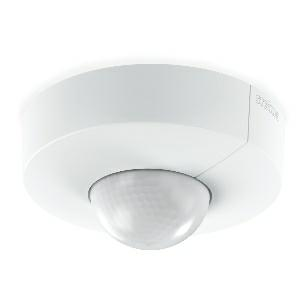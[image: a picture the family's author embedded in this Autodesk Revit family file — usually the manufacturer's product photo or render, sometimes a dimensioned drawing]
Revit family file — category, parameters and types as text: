
# Revit family: is_345_033859
name_source: partatom
category: Elektroinstallationen
revit_build: Autodesk Revit 2016 (Build: 20190508_0715(x64)
units: mm (PartAtom-declared; Revit-internal decimal feet)

## family parameters
Basisbauteil = Fläche
Beim Laden mit Abzugskörper schneiden = Nein
Bemaßung runder Anschluss = Durchmesser verwenden
Beschriftungsausrichtung beibehalten = Nein
Gemeinsam genutzt = Nein
Raumberechnungspunkt = Nein
Teiletyp = Normal

## types (1)
- IS 345
    Apparent Load = 0 VA
    Beschreibung = Type: Motion detectors; Dimensions (Ø x H): 126 x 65 mm; Mains power supply: 220 – 240 V / 50 – 60 Hz; Sensor Technology: passive infrared; Application, place: Outdoors, Indoors; Application, room: corridor / aisle, multi-storey / underground car park, outdoors, hotel room; Installation site: ceiling; Installation: Surface wiring; Switching zones: 280 switching zones; Electronic scalability: No; Mechanical scalability: No; Mounting height: 2,50 – 5,00 m; Optimum mounting height: 2,8 m; Detection angle: 360 °; Angle of aperture: 45 °; Sneak-by guard: Yes; Capability of masking out individual segments: Yes; Reach, radial: 12 x 6 m (72 m²); Reach, tangential: 23 x 6 m (138 m²); Twilight setting TEACH: Yes; Twilight setting: 2 – 1000 lx; Time setting: 5 sec – 15 min; Control output, Dali: Broadcast 1x30 electronic ballasts; Constant-lighting control: Yes; Basic light level function: Yes; Basic light level function in per cent: 10 – 50 %; Basic light level function time: 1-30 min, all night; Basic light level function percentage, from: 10 %; Basic light level function percentage, up to: 50 %; Functions: Normal / test mode, Manual ON / ON-OFF, Constant-lighting control ON-OFF; Settings via: Remote control, Potentiometers, Smart Remote; With remote control: No; Interconnection: Yes; IP-rating: IP54; Material: Plastic; Ambient temperature: -20 – 50 °C; Colour: white; Colour, RAL: 9003; Manufacturer's Warranty: 5 years; Version: DALI-2 Application Controller - surface, rd.; PU1, EAN: 4007841033859
    Height = 0 mm  [stored 0 ft]
    Hersteller = Steinel
    Length = 126 mm
    Maximum range = 11.589 m
    ModVariant = Nein
    Modell = 033859
    Mounting Place = Ceiling
    Mounting Type = Surface mounted
    Number of Poles = 1
    OnlyDefault = Ja
    Power Factor = 1
    Product Name = IS 345
    Product group = Sensor-switched outdoor light
    ProductGroupID = 3
    Protection Class = Protection class
    Protection Degree = IP 54
    RlxData = <blob elided: 156845 chars, md5=6c22403c>
    Sensor characteristics = Stretched
    Sensor type = Passive (infrared)
    SensorDataFile = <blob elided: 5885 chars, md5=98bccc25>
    Type of entry = Motion
    Typenbild = produkt1_033859.jpg
    Typenkommentare = Product without accessories
    URL = http://relux.com
    VarID = ---
    Voltage = 0 V
    Vorgabe-Ansicht = 1800 mm
    Weight = 0.00 kg
    Width = 0 mm  [stored 0 ft]

note: [stored X ft] marks values corroborated as IEEE doubles in the binary element streams (Revit-internal decimal feet)

## geometry (parser evidence)
native form markers: Blend x4, Sweep x19
no freeform markers — native parametric forms only
